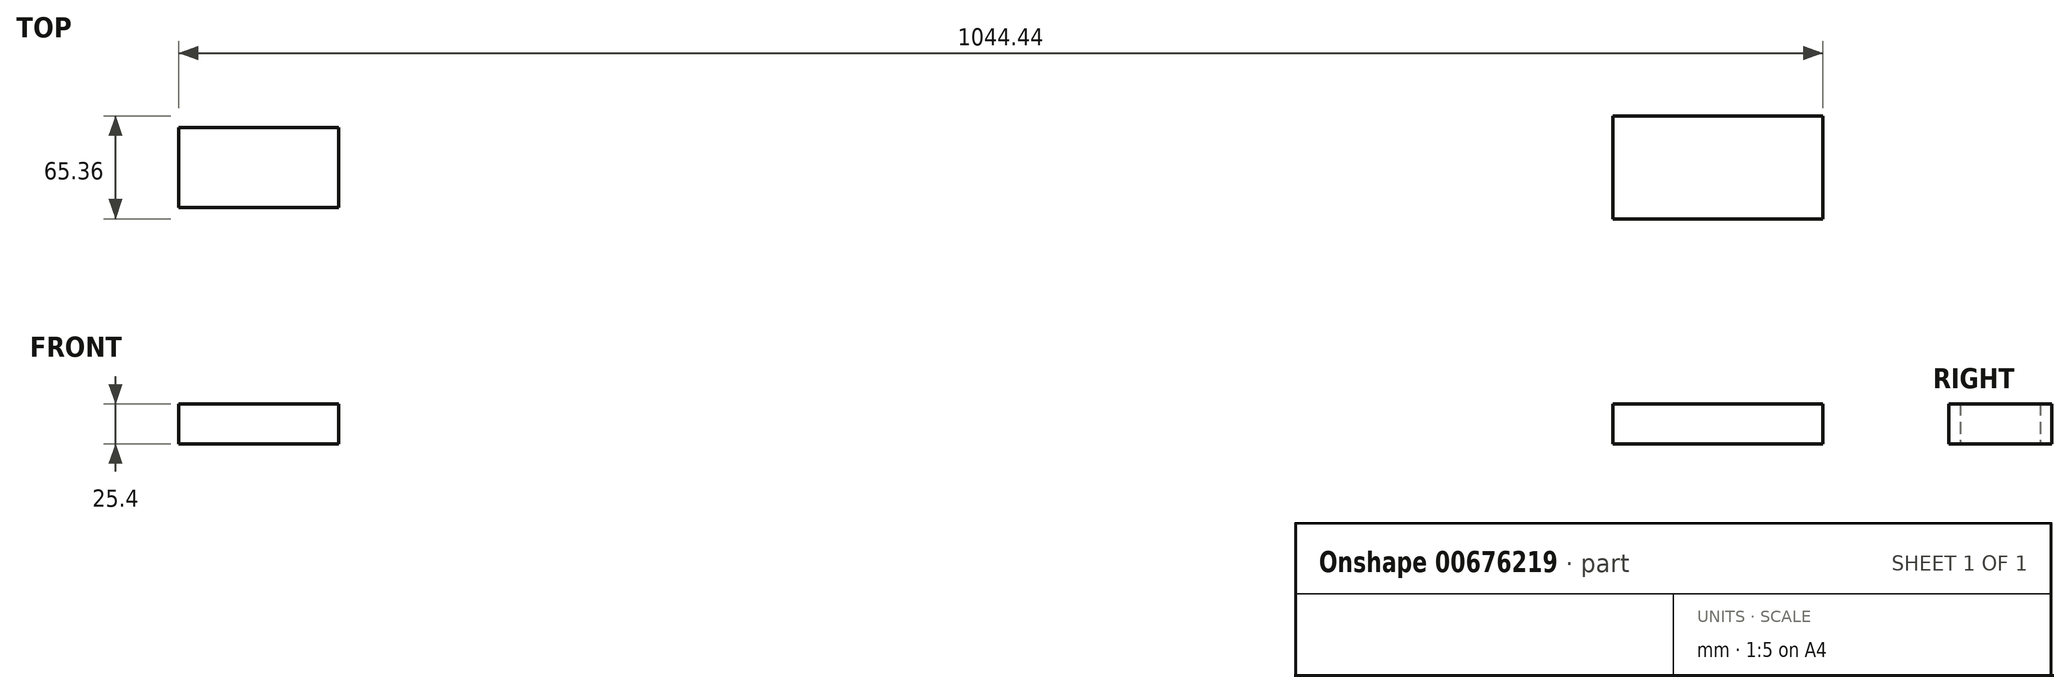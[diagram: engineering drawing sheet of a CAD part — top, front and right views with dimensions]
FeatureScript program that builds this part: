
annotation { "Feature Type Name" : "Feature", "Feature Type Description" : "" }
export const myFeature = defineFeature(function(context is Context, id is Id, definition is map)
    precondition{}
    {
        {
            var Q0;
            Q0=qCreatedBy(makeId("Top.planeOp"),FACE);
            var sketch = newSketch(context, id + "F0", { "sketchPlane" : qUnion([Q0])});
            skLineSegment(sketch, "E0.bottom", {"start": v(993.64, 32.68) * mm, "end": v(860.35, 32.68) * mm});
            skLineSegment(sketch, "E0.top", {"start": v(993.64, -32.68) * mm, "end": v(860.35, -32.68) * mm});
            skLineSegment(sketch, "E0.left", {"start": v(993.64, 32.68) * mm, "end": v(993.64, -32.68) * mm});
            skLineSegment(sketch, "E0.right", {"start": v(860.35, 32.68) * mm, "end": v(860.35, -32.68) * mm});
            skPoint(sketch, "E0.middle", {"position": v(927, 0) * mm});
            skLineSegment(sketch, "E1.bottom", {"start": v(50.8, 25.4) * mm, "end": v(-50.8, 25.4) * mm});
            skLineSegment(sketch, "E1.top", {"start": v(50.8, -25.4) * mm, "end": v(-50.8, -25.4) * mm});
            skLineSegment(sketch, "E1.left", {"start": v(50.8, 25.4) * mm, "end": v(50.8, -25.4) * mm});
            skLineSegment(sketch, "E1.right", {"start": v(-50.8, 25.4) * mm, "end": v(-50.8, -25.4) * mm});
            skPoint(sketch, "E1.middle", {"position": v(0, 0) * mm});
            skSolve(sketch);
        }
        {
            var Q0;
            Q0 = qSketchRegion(id + "F0", true);
            extrude(context, id + "F1", {"entities" : qUnion([Q0]), "depth" : 25.4 * mm, "offsetDistance" : 25.4 * mm});
        }
    });
